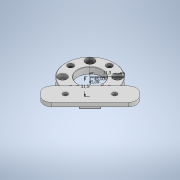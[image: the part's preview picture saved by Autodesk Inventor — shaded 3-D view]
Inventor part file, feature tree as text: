
AUTODESK INVENTOR PART (.ipt)
format: ipt  version: 2020 (Build 240168000, 168)  size: 352,768 bytes
history: native  units: in
note: dims shown in document units (in); Inventor stores cm internally (conversion verified against a paired STEP export)
features: sketch x11, extrude x8, plane x5, fillet x5, chamfer x4, pattern_circular x3, hole x2, mirror x1
ambient origin geometry x8: Origin, YZ Plane, XZ Plane, XY Plane, X Axis, Y Axis, Z Axis, Center Point
bodies: Solid1 (feature_tree)
feature tree (39):
  extrude  "Extrusion1"  Depth=0.1969in TaperAngle=0.0deg
  extrude  "Extrusion2"  Depth=0.1969in TaperAngle=0.0deg
  hole  "Hole1"  [1 undecoded]
  plane  "Work Plane1"
  sketch  "Sketch6"  dims[d27=1.2402in d29=1.2402in]
  plane  "Work Plane2"
  extrude  "Extrusion3"  Depth=1.2402in
  plane  "Work Plane3"
  extrude  "Extrusion4"  Depth=0.7874in
  extrude  "Extrusion5"  Depth=0.1969in
  fillet  "Fillet1"  Radius=0.1969in
  pattern_circular  "Circular Pattern2"  Count=9  [1 undecoded]
  fillet  "Fillet2"  Radius=0.1969in
  fillet  "Fillet3"  Radius=1.0236in
  fillet  "Fillet4"  Radius=0.3937in
  fillet  "Fillet5"  Radius=1.5748in
  sketch  "Sketch13"  dims[d38=0.8071in d39=0.0in d40=3.5433in d41=0.1969in d42=1.0236in d43=0.0in d44=0.3937in d45=1.5748in d46=360.0deg]
  plane  "Work Plane5"
  extrude  "Extrusion6"  Depth=0.1969in
  hole  "Hole4"  [1 undecoded]
  plane  "Work Plane6"
  mirror  "Mirror1"
  sketch  "Sketch19"  dims[d64=0.2598in d65=0.9843in d66=0.3937in d67=0.0in d68=0.1378in d69=0.2362in d70=0.2362in d71=0.0787in d72=90.0deg d73=0.315in d74=0.8108in d75=0.8858in d82=0.1378in d83=0.0in d85=0.1969in d89=0.0197in d90=0.0787in d91=45.0deg d92=0.0197in d93=0.0787in d94=45.0deg d95=0.0197in d96=0.0787in d97=45.0deg d98=0.3937in d99=0.1969in d100=0.0in d101=1.5748in d102=360.0deg d104=0.3937in d109=0.2362in d110=0.0in d111=1.5748in d112=360.0deg d114=0.0197in d115=0.0787in d116=45.0deg d84=0.0197in]
  extrude  "Extrusion10"  TaperAngle=45.0deg  [1 undecoded]
  chamfer  "Chamfer4"  Distance=0.9843in
  chamfer  "Chamfer5"  Distance=0.3937in
  chamfer  "Chamfer6"  Distance=0.8858in
  extrude  "Extrusion7"  Depth=0.2362in TaperAngle=0.0deg
  pattern_circular  "Circular Pattern5"  [2 undecoded]
  chamfer  "Chamfer7"  Distance=0.0197in Angle=45.0deg
  pattern_circular  "Circular Pattern6"  Angle=45.0deg  [1 undecoded]
  sketch  "Sketch1"  dims[d0=2.4803in d1=0.1969in d2=0.0in]
  sketch  "Sketch2"  dims[d3=1.2402in d4=0.1969in d5=0.0in]
  sketch  "Sketch3"  dims[d9=0.2598in d10=0.2362in d11=0.4094in d12=0.1575in d13=90.0deg d14=0.315in d15=0.8108in d16=0.9843in]
  sketch  "Sketch11"  dims[d30=45.0deg d31=0.7874in]
  sketch  "Sketch12"  dims[d32=0.4724in d33=0.2953in d34=0.0in d35=0.0in d36=0.7874in d37=0.1969in]
  sketch  "Sketch15"  dims[d48=0.1969in d49=0.1969in]
  sketch  "Sketch16"  dims[d50=0.0394in d54=0.1181in]
  sketch  "Sketch18"  dims[d55=1.2402in d56=45.0deg]
note: 7 required parameter values undecoded (feature->parameter linkage not recoverable at this tier; creation-order binding heuristic only, values carry confidence <= 0.55)
